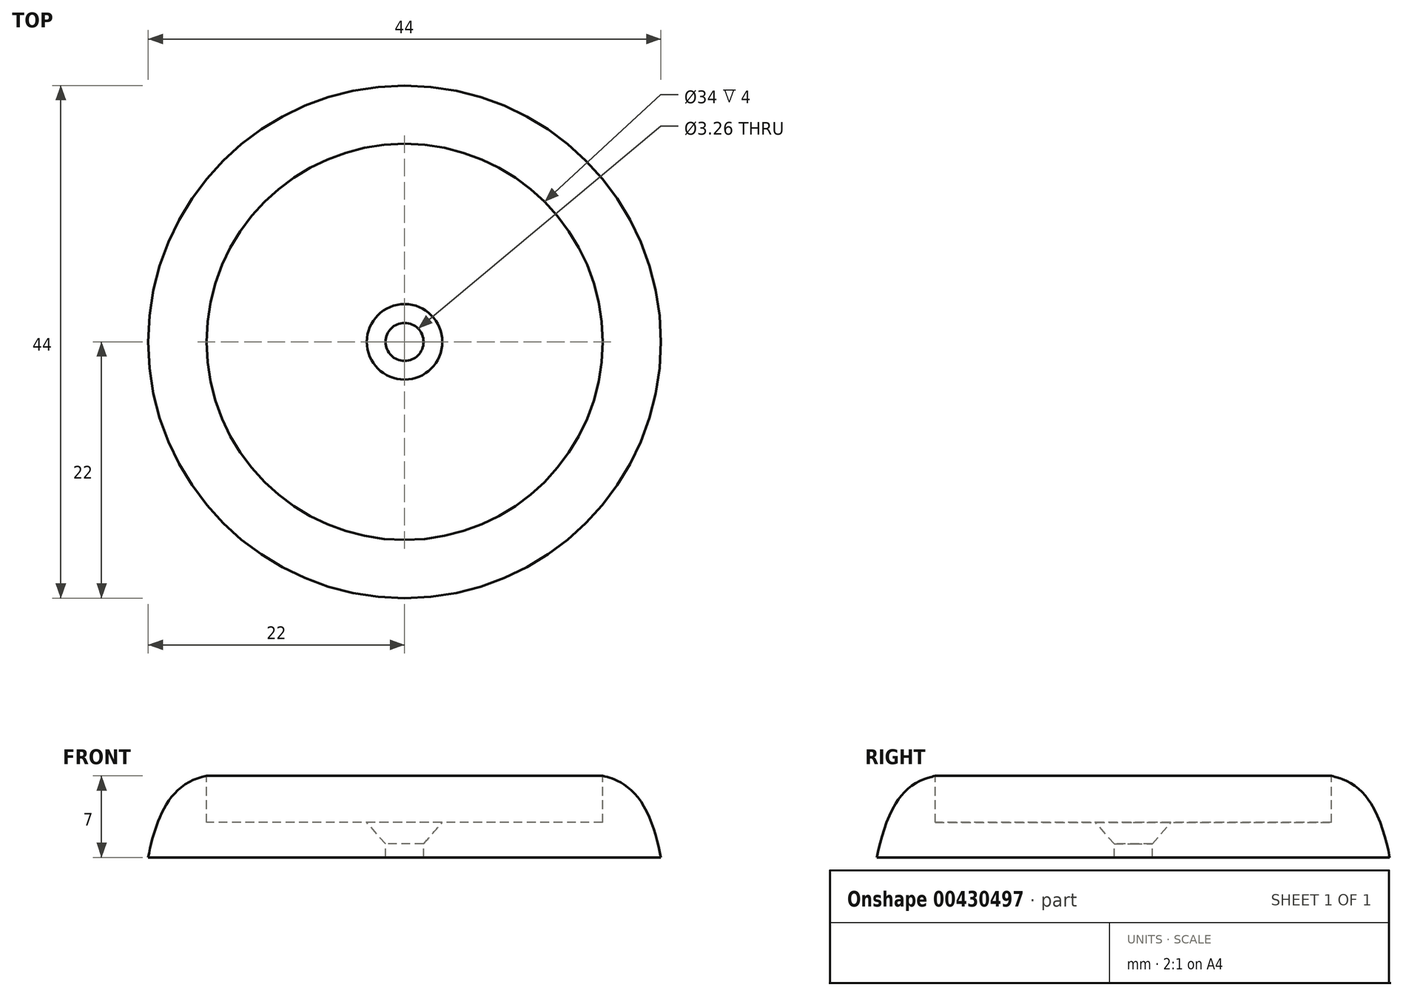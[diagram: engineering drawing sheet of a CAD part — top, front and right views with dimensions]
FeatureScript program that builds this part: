
annotation { "Feature Type Name" : "Feature", "Feature Type Description" : "" }
export const myFeature = defineFeature(function(context is Context, id is Id, definition is map)
    precondition{}
    {
        {
            var Q0;
            Q0=qCreatedBy(makeId("Front.planeOp"),FACE);
            var sketch = newSketch(context, id + "F0", { "sketchPlane" : qUnion([Q0])});
            skLineSegment(sketch, "E0", {"start": v(0, 0) * mm, "end": v(-17, 0) * mm});
            skLineSegment(sketch, "E1", {"start": v(-17, 0) * mm, "end": v(-17, 4) * mm});
            skLineSegment(sketch, "E2", {"start": v(0, 0) * mm, "end": v(0, -3) * mm});
            skLineSegment(sketch, "E3", {"start": v(0, -3) * mm, "end": v(-17, -3) * mm});
            skLineSegment(sketch, "E4", {"start": v(-17, -3) * mm, "end": v(-22, -3) * mm});
            skFitSpline(sketch, "E5", {"points": [v(-22, -3) * mm, v(-20.08, 2.08) * mm, v(-17.93, 3.73) * mm, v(-17, 4) * mm], "startDerivative": vector(1.74, 10.17) * mm, "endDerivative": vector(4.8, 1.41) * mm});
            skSolve(sketch);
        }
        {
            var Q0;
            Q0=makeQuery(id+"F0.imprint","IMPRINT",FACE,{"disambiguationData":[TD([[makeQuery(id+"F0.imprint","IMPRINT",EDGE,{"derivedFrom":sQuery(id+"F0.wireOp",EDGE,"E0")}),1.0]])]});
            var Q1;
            Q1=sQuery(id+"F0.wireOp",EDGE,"E2");
            revolve(context, id + "F1", {"entities" : qUnion([Q0]), "axis" : qUnion([Q1]), "revolveType" : RevolveType.FULL});
        }
        {
            var Q0;
            Q0=makeQuery(id+"F1.opRevolve","SWEPT_FACE",FACE,{"disambiguationData":[OSD([sQuery(id+"F0.wireOp",EDGE,"E0")])]});
            var sketch = newSketch(context, id + "F2", { "sketchPlane" : qUnion([Q0])});
            skCircle(sketch, "E6", {"center": v(0, 0) * mm, "radius": 10 * mm});
            skSolve(sketch);
        }
        {
            var Q0;
            Q0=sQuery(id+"F2.wireOp",VERTEX,"E6.center");
            var Q1;
            Q1=makeQuery(id+"F1.opRevolve","SWEPT_BODY",BODY,{"disambiguationData":[OSD([sQuery(id+"F0.wireOp",EDGE,"E0"),sQuery(id+"F0.wireOp",EDGE,"E1"),sQuery(id+"F0.wireOp",EDGE,"E2"),sQuery(id+"F0.wireOp",EDGE,"E3"),sQuery(id+"F0.wireOp",EDGE,"E4"),sQuery(id+"F0.wireOp",EDGE,"E5")])]});
            hole(context, id + "F3", {"style" : HoleStyle.C_SINK, "endStyle" : HoleEndStyle.THROUGH, "standardTappedOrClearance" : lookupTablePath({ "standard" : "ANSI", "fit" : "Normal (ASME)", "size" : "#4", "type" : "Clearance" }), "standardBlindInLast" : lookupTablePath({ "fit" : "Free", "standard" : "ANSI", "size" : "#4", "type" : "Clearance" }), "holeDiameter" : 3.26 * mm, "cSinkDiameter" : 6.48 * mm, "cSinkAngle" : 82 * degree, "isTappedThrough" : true, "tappedDepth" : 12 * mm, "tapClearance" : 3, "locations" : qUnion([Q0]), "scope" : qUnion([Q1])});
        }
    });
